# Revit family: KLA181 & AF12 - Freespace
name_source: partatom
category: Communication Devices
revit_build: Autodesk Revit 2017 (Build: 20190508_0315(x64)
units: mm (PartAtom-declared; Revit-internal decimal feet)

## family parameters
Always vertical = No
Cut with Voids When Loaded = No
Maintain Annotation Orientation = No
Part Type = Normal
Room Calculation Point = No
Round Connector Dimension = Use Diameter
Shared = No
Work Plane-Based = Yes

## types (3) — shared parameters
Depth = 653 mm  [stored 2.14239 ft]
Description = 18" Ported Subwoofer
Height = 547 mm
Manufacturer = QSC
Manufacturer URL = www.qsc.com
Model = KLA181
Product Documentation Link = https://www.qsc.com
Product Page URL = https://www.qsc.com
SPL Max = 135
URL = https://www.qsc.com
Voltage AC = 100-240VAC, 50-60Hz
Weight Product (kg) = 47.2
Weight Product (lb) = 104
Width = 594 mm  [stored 1.94882 ft]
zero-valued in all types: Default Elevation

## per-type parameters (varying)
| type | AF12 Orientation | Show AF12 |
| KLA181 | QSC AF12 : Position C | No |
| KLA181 w/ AF12 Up Tilt | QSC AF12 : Position D | Yes |
| KLA181 w/ AF12 Down Tilt | QSC AF12 : Position C | Yes |

note: [stored X ft] marks values corroborated as IEEE doubles in the binary element streams (Revit-internal decimal feet)

## geometry (parser evidence)
native form markers: Blend x3, Sweep x14
no freeform markers — native parametric forms only
